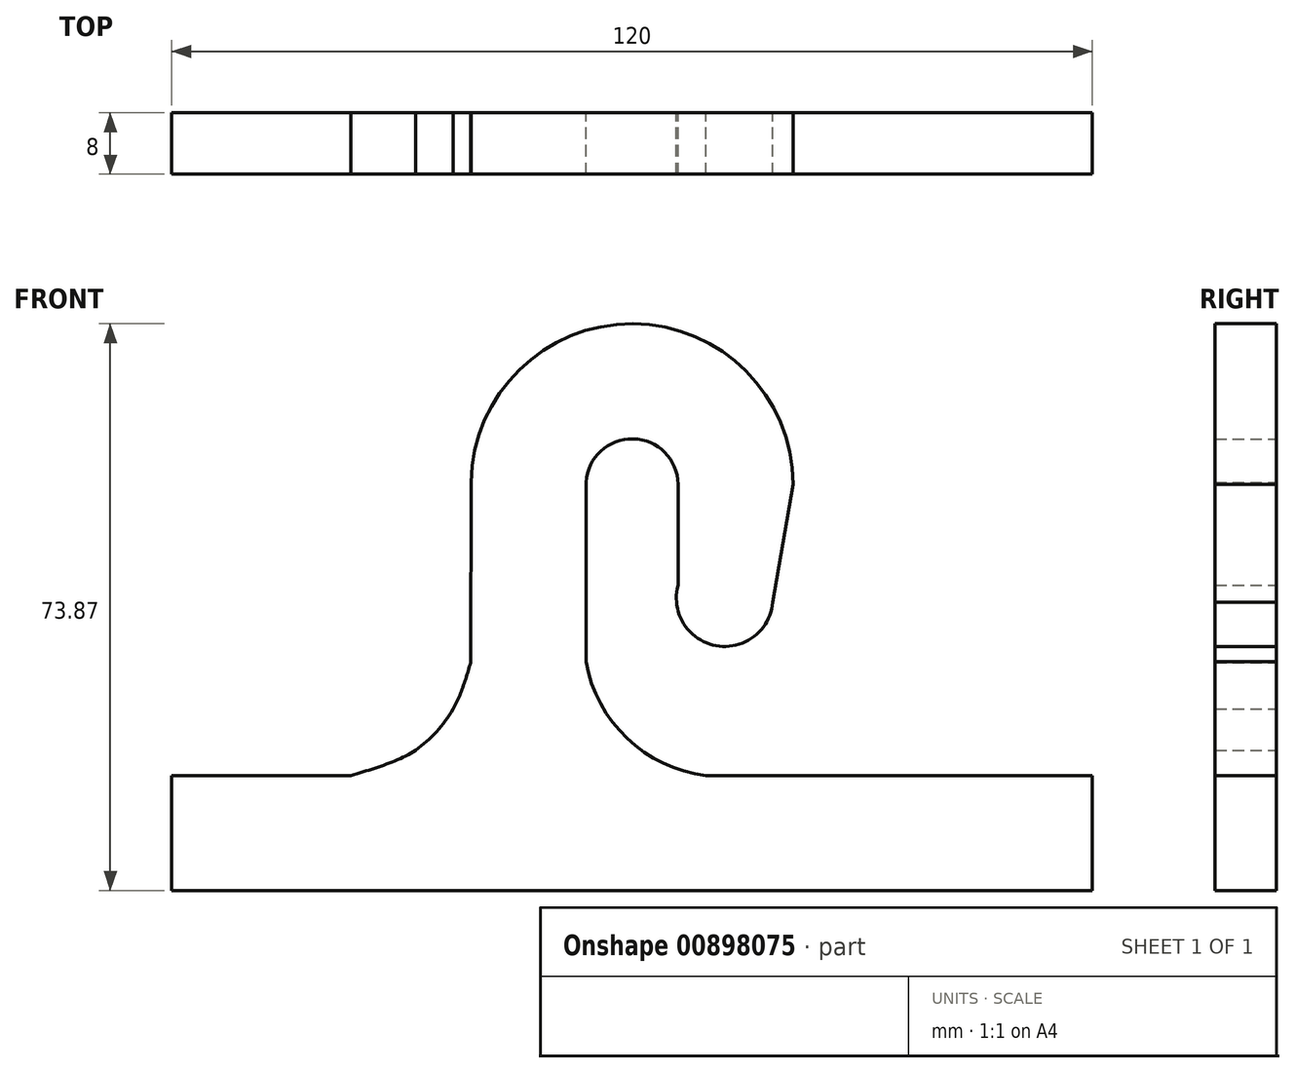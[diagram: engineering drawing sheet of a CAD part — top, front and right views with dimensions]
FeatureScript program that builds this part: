
annotation { "Feature Type Name" : "Feature", "Feature Type Description" : "" }
export const myFeature = defineFeature(function(context is Context, id is Id, definition is map)
    precondition{}
    {
        {
            var Q0;
            Q0=qCreatedBy(makeId("Front.planeOp"),FACE);
            var sketch = newSketch(context, id + "F0", { "sketchPlane" : qUnion([Q0])});
            skArc(sketch, "E0", {"start": v(21, 21.38) * mm, "mid": v(0.12, 42.28) * mm, "end": v(-21, 21.63) * mm});
            skArc(sketch, "E1", {"start": v(6, 21.38) * mm, "mid": v(-0.22, 27.28) * mm, "end": v(-6, 20.94) * mm});
            skLineSegment(sketch, "E2.right", {"start": v(0.64, 0.48) * mm, "end": v(0.64, 0.3) * mm});
            skArc(sketch, "E3", {"start": v(6, 21.2) * mm, "mid": v(-0.12, 27.28) * mm, "end": v(-6, 20.94) * mm});
            skLineSegment(sketch, "E4.bottom", {"start": v(6, 21.63) * mm, "end": v(6, 21.63) * mm});
            skLineSegment(sketch, "E4.left", {"start": v(-6, 21.63) * mm, "end": v(-6, 1.16) * mm});
            skLineSegment(sketch, "E4.right", {"start": v(6, 21.63) * mm, "end": v(6, 8.2) * mm});
            skLineSegment(sketch, "E5.left", {"start": v(-6, 21.63) * mm, "end": v(-6, -1.75) * mm});
            skPoint(sketch, "E6.orphan", {"position": v(6, 1.16) * mm});
            skArc(sketch, "E7", {"start": v(6, 8.15) * mm, "mid": v(10.98, 0.32) * mm, "end": v(18.35, 5.97) * mm});
            skLineSegment(sketch, "E8", {"start": v(21, 21.38) * mm, "end": v(18.17, 4.94) * mm});
            skArc(sketch, "E9", {"start": v(-6, -1.75) * mm, "mid": v(-0.64, -11.76) * mm, "end": v(9.63, -16.6) * mm});
            skArc(sketch, "E10.MirrorCS", {"start": v(-21.01, -1.75) * mm, "mid": v(-21.03, -1.82) * mm, "end": v(-21.04, -1.89) * mm});
            skLineSegment(sketch, "E11.bottom", {"start": v(60, -31.6) * mm, "end": v(-60, -31.6) * mm});
            skLineSegment(sketch, "E11.top", {"start": v(60, -16.6) * mm, "end": v(9.63, -16.6) * mm});
            skLineSegment(sketch, "E11.left", {"start": v(60, -31.6) * mm, "end": v(60, -16.6) * mm});
            skLineSegment(sketch, "E11.right", {"start": v(-60, -31.6) * mm, "end": v(-60, -16.6) * mm});
            skLineSegment(sketch, "E12.trimOffspring", {"start": v(-36.64, -16.6) * mm, "end": v(-60, -16.6) * mm});
            skLineSegment(sketch, "E13.left", {"start": v(-21, 21.63) * mm, "end": v(-21, -1.75) * mm});
            skLineSegment(sketch, "E14", {"start": v(-21.01, -1.75) * mm, "end": v(-21, 21.63) * mm});
            skLineSegment(sketch, "E15", {"start": v(-21.01, -1.75) * mm, "end": v(-21, -1.75) * mm});
            skPoint(sketch, "E16.start.orphan", {"position": v(0, -31.6) * mm});
            skLineSegment(sketch, "E17.bottom", {"start": v(-60, -16.6) * mm, "end": v(-36.64, -16.6) * mm});
            skLineSegment(sketch, "E17.top", {"start": v(-60, -31.6) * mm, "end": v(60, -31.6) * mm});
            skLineSegment(sketch, "E17.left", {"start": v(-60, -16.6) * mm, "end": v(-60, -31.6) * mm});
            skLineSegment(sketch, "E17.right", {"start": v(60, -16.6) * mm, "end": v(60, -31.6) * mm});
            skFitSpline(sketch, "E18", {"points": [v(-36.64, -16.6) * mm, v(-28.23, -13.3) * mm, v(-23.31, -7.95) * mm, v(-21, -1.75) * mm], "startDerivative": vector(24.87, 7.24) * mm, "endDerivative": vector(6, 20.37) * mm});
            skLineSegment(sketch, "E19", {"start": v(-21, -1.75) * mm, "end": v(-21, 21.63) * mm});
            skLineSegment(sketch, "E20", {"start": v(6, 8.2) * mm, "end": v(6.01, 8.2) * mm});
            skArc(sketch, "E21", {"start": v(6.01, 8.2) * mm, "mid": v(10.96, 0.32) * mm, "end": v(18.35, 5.97) * mm});
            skLineSegment(sketch, "E22.trimOffspring", {"start": v(9.63, -16.6) * mm, "end": v(60, -16.6) * mm});
            skFitSpline(sketch, "E23.trimOffspring", {"points": [v(-36.64, -16.6) * mm, v(-28.23, -13.3) * mm, v(-23.31, -7.95) * mm, v(-21, -1.75) * mm], "startDerivative": vector(24.87, 7.24) * mm, "endDerivative": vector(6, 20.37) * mm});
            skArc(sketch, "E24.trimOffspring", {"start": v(-23.31, -7.95) * mm, "mid": v(-25.5, -10.88) * mm, "end": v(-28.23, -13.3) * mm});
            skSolve(sketch);
        }
        {
            var Q0;
            Q0 = qSketchRegion(id + "F0", true);
            extrude(context, id + "F1", {"entities" : qUnion([Q0]), "depth" : 8 * mm, "offsetDistance" : 25 * mm});
        }
    });
